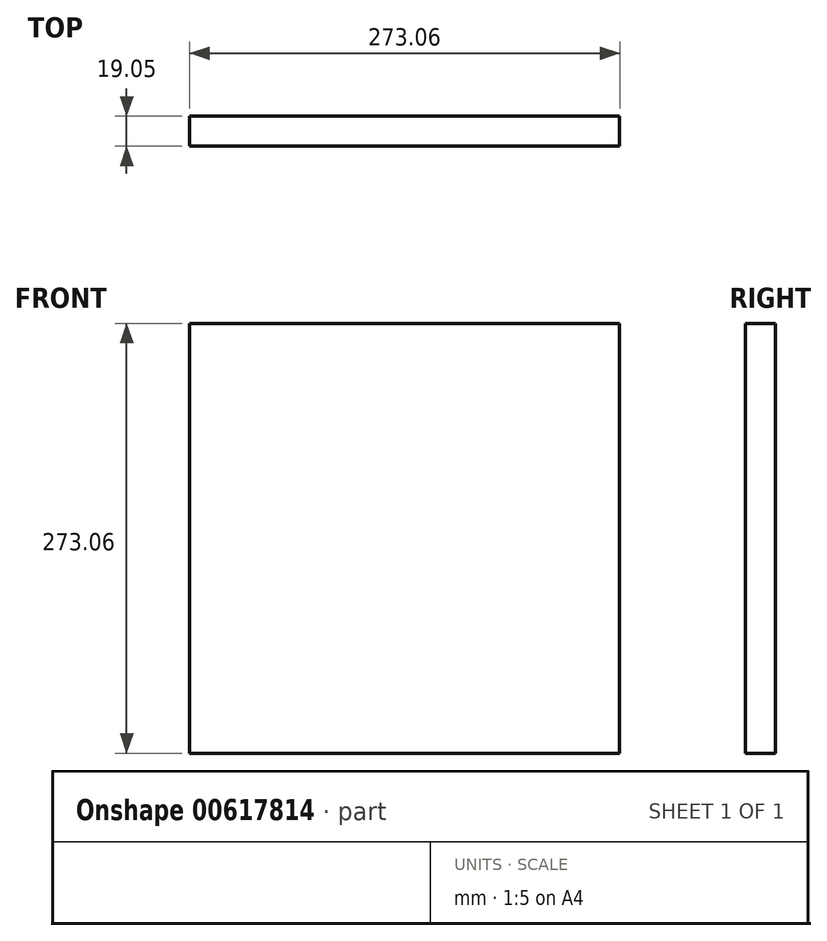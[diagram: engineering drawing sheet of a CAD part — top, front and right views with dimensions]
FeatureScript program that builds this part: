
annotation { "Feature Type Name" : "Feature", "Feature Type Description" : "" }
export const myFeature = defineFeature(function(context is Context, id is Id, definition is map)
    precondition{}
    {
        {
            var Q0;
            Q0=qCreatedBy(makeId("Front.planeOp"),FACE);
            var sketch = newSketch(context, id + "F0", { "sketchPlane" : qUnion([Q0])});
            skLineSegment(sketch, "E0.bottom", {"start": v(-136.53, 136.53) * mm, "end": v(136.53, 136.53) * mm});
            skLineSegment(sketch, "E0.top", {"start": v(-136.53, -136.52) * mm, "end": v(136.53, -136.52) * mm});
            skLineSegment(sketch, "E0.left", {"start": v(-136.52, 136.53) * mm, "end": v(-136.53, -136.52) * mm});
            skLineSegment(sketch, "E0.right", {"start": v(136.53, 136.53) * mm, "end": v(136.53, -136.52) * mm});
            skPoint(sketch, "E0.middle", {"position": v(0, 0) * mm});
            skSolve(sketch);
        }
        {
            var Q0;
            Q0=makeQuery(id+"F0.imprint","IMPRINT",FACE,{"disambiguationData":[TD([[makeQuery(id+"F0.imprint","IMPRINT",EDGE,{"derivedFrom":sQuery(id+"F0.wireOp",EDGE,"E0.bottom")}),-1.0]])]});
            extrude(context, id + "F1", {"entities" : qUnion([Q0]), "depth" : 19.05 * mm, "offsetDistance" : 25.4 * mm});
        }
    });
